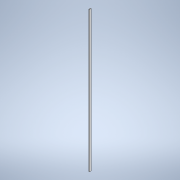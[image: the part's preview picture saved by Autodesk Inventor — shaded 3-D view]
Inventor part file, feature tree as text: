
AUTODESK INVENTOR PART (.ipt)
format: ipt  version: 2021 (Build 250183000, 183)  size: 93,696 bytes
history: native  units: mm
features: extrude x1, sketch x1
ambient origin geometry x8: Origin, YZ Plane, XZ Plane, XY Plane, X Axis, Y Axis, Z Axis, Center Point
bodies: Solid1 (feature_tree)
feature tree (2):
  extrude  "Extrusion1"  Depth=20.0mm
  sketch  "Sketch1"  dims[d0=10.0mm d1=20.0mm d2=1944.0mm d3=0.0mm]
